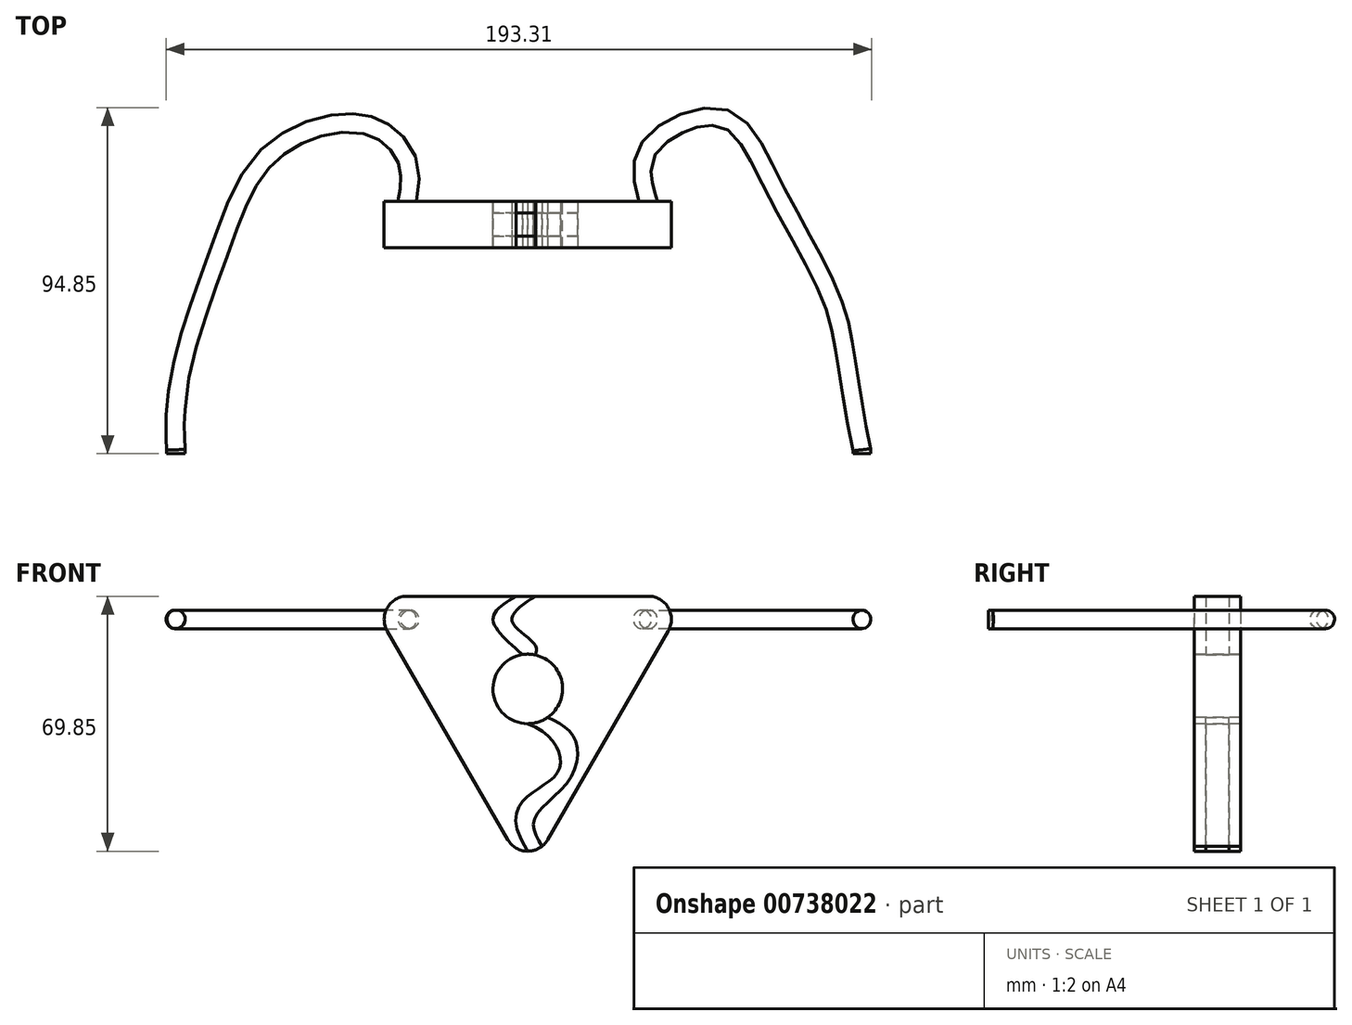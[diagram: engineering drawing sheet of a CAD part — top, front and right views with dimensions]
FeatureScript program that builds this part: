
annotation { "Feature Type Name" : "Feature", "Feature Type Description" : "" }
export const myFeature = defineFeature(function(context is Context, id is Id, definition is map)
    precondition{}
    {
        {
            var Q0;
            Q0=qCreatedBy(makeId("Front.planeOp"),FACE);
            var sketch = newSketch(context, id + "F0", { "sketchPlane" : qUnion([Q0])});
            skCircle(sketch, "E0", {"center": v(0, 0) * mm, "radius": 9.53 * mm});
            skLineSegment(sketch, "E1", {"start": v(-33, 25.4) * mm, "end": v(33, 25.4) * mm});
            skLineSegment(sketch, "E2", {"start": v(38.5, 15.88) * mm, "end": v(5.5, -41.27) * mm});
            skLineSegment(sketch, "E3", {"start": v(-5.5, -41.27) * mm, "end": v(-38.5, 15.87) * mm});
            skPoint(sketch, "E4.visualSharp", {"position": v(-44, 25.4) * mm});
            skArc(sketch, "E4.filletArc", {"start": v(-33, 25.4) * mm, "mid": v(-38.5, 22.23) * mm, "end": v(-38.5, 15.88) * mm});
            skPoint(sketch, "E5.visualSharp", {"position": v(44, 25.4) * mm});
            skArc(sketch, "E5.filletArc", {"start": v(38.5, 15.88) * mm, "mid": v(38.5, 22.23) * mm, "end": v(33, 25.4) * mm});
            skPoint(sketch, "E6.visualSharp", {"position": v(0, -50.8) * mm});
            skArc(sketch, "E6.filletArc", {"start": v(-5.5, -41.27) * mm, "mid": v(0, -44.45) * mm, "end": v(5.5, -41.27) * mm});
            skPoint(sketch, "E7.2.internal.snap0", {"position": v(0, 25.4) * mm});
            skFitSpline(sketch, "E8", {"points": [v(0, -9.53) * mm, v(7.61, -23.64) * mm, v(0, -44.45) * mm], "startDerivative": vector(51.93, -20.61) * mm, "endDerivative": vector(51.79, -79.45) * mm});
            skFitSpline(sketch, "E9", {"points": [v(2.14, 25.4) * mm, v(-4.25, 18.42) * mm, v(2.32, 11.47) * mm, v(2.1, 9.3) * mm, v(2.22, 9.26) * mm], "startDerivative": vector(-27.78, -18.05) * mm, "endDerivative": vector(3.6, 0.43) * mm});
            skFitSpline(sketch, "E10", {"points": [v(-3.19, 25.4) * mm, v(-9.52, 19.35) * mm, v(-1.43, 9.42) * mm], "startDerivative": vector(-20.5, -12.29) * mm, "endDerivative": vector(22.65, -19.45) * mm});
            skFitSpline(sketch, "E11", {"points": [v(3.94, -43.08) * mm, v(1.78, -35.75) * mm, v(11.53, -24.63) * mm, v(12.73, -13.34) * mm, v(5.5, -7.78) * mm], "startDerivative": vector(-21.2, 34.46) * mm, "endDerivative": vector(-37.55, 18.63) * mm});
            skSolve(sketch);
        }
        {
            var Q0;
            Q0 = qSketchRegion(id + "F0", true);
            extrude(context, id + "F1", {"entities" : qUnion([Q0]), "endBound" : BoundingType.SYMMETRIC, "depth" : 12.7 * mm, "offsetDistance" : 25.4 * mm});
        }
        {
            var Q0;
            {var subQ0=sQuery(id+"F0.wireOp",EDGE,"E10");Q0=makeQuery(id+"F0.imprint","IMPRINT",FACE,{"disambiguationData":[TD([[makeQuery(id+"F0.imprint","IMPRINT",EDGE,{"derivedFrom":subQ0}),1.0]])]});}
            var Q1;
            {var subQ0=sQuery(id+"F0.wireOp",EDGE,"E8");Q1=makeQuery(id+"F0.imprint","IMPRINT",FACE,{"disambiguationData":[TD([[makeQuery(id+"F0.imprint","IMPRINT",EDGE,{"derivedFrom":subQ0}),1.0]])]});}
            extrude(context, id + "F2", {"entities" : qUnion([Q0, Q1]), "operationType" : NewBodyOperationType.REMOVE, "endBound" : BoundingType.SYMMETRIC, "oppositeDirection" : true, "depth" : 25.4 * mm, "offsetDistance" : 25.4 * mm});
        }
        {
            var Q0;
            {var subQ0=sQuery(id+"F0.wireOp",EDGE,"E10");Q0=makeQuery(id+"F0.imprint","IMPRINT",FACE,{"disambiguationData":[TD([[makeQuery(id+"F0.imprint","IMPRINT",EDGE,{"derivedFrom":subQ0}),1.0]])]});}
            var Q1;
            {var subQ0=sQuery(id+"F0.wireOp",EDGE,"E8");Q1=makeQuery(id+"F0.imprint","IMPRINT",FACE,{"disambiguationData":[TD([[makeQuery(id+"F0.imprint","IMPRINT",EDGE,{"derivedFrom":subQ0}),1.0]])]});}
            extrude(context, id + "F3", {"entities" : qUnion([Q0, Q1]), "endBound" : BoundingType.SYMMETRIC, "depth" : 6.35 * mm, "offsetDistance" : 25.4 * mm});
        }
        {
            var Q0;
            {var subQ0=sQuery(id+"F0.wireOp",EDGE,"E4.filletArc");var subQ1=sQuery(id+"F0.wireOp",EDGE,"E1");var subQ2=sQuery(id+"F0.wireOp",EDGE,"E3");var subQ3=sQuery(id+"F0.wireOp",EDGE,"E0");var subQ4=sQuery(id+"F0.wireOp",EDGE,"E6.filletArc");Q0=makeQuery(id+"F2.boolean.opBoolean","SPLIT",FACE,{"disambiguationData":[TD([makeQuery(id+"F1.opExtrude","SWEPT_FACE",FACE,{"disambiguationData":[OSD([subQ2])]})])],"derivedFrom":makeQuery(id+"F1.opExtrude","CAP_FACE",FACE,{"disambiguationData":[OSD([subQ3,subQ1,sQuery(id+"F0.wireOp",EDGE,"E2"),subQ2,subQ0,sQuery(id+"F0.wireOp",EDGE,"E5.filletArc"),subQ4])],"isStart":true})});}
            var sketch = newSketch(context, id + "F4", { "sketchPlane" : qUnion([Q0])});
            skCircle(sketch, "E12", {"center": v(33, 19.05) * mm, "radius": 2.54 * mm});
            skSolve(sketch);
        }
        {
            var Q0;
            Q0=qCreatedBy(makeId("Top.planeOp"),FACE);
            var sketch = newSketch(context, id + "F5", { "sketchPlane" : qUnion([Q0])});
            skPoint(sketch, "E13.0", {"position": v(-33, 6.35) * mm});
            skLineSegment(sketch, "E14.0", {"start": v(-35.54, 6.35) * mm, "end": v(-30.46, 6.35) * mm});
            skFitSpline(sketch, "E15", {"points": [v(-33, 6.35) * mm, v(-33, 17.32) * mm, v(-43.99, 27.32) * mm, v(-69.53, 20.42) * mm, v(-84, -5.7) * mm, v(-94.93, -39.8) * mm, v(-96.4, -61.63) * mm], "startDerivative": vector(15.54, 93.73) * mm, "endDerivative": vector(8.7, -120.43) * mm});
            skLineSegment(sketch, "E16", {"start": v(-96.4, -61.63) * mm, "end": v(-96.4, -64.8) * mm});
            skSolve(sketch);
        }
        {
            var Q0;
            Q0=makeQuery(id+"F4.imprint","IMPRINT",FACE,{"disambiguationData":[TD([[makeQuery(id+"F4.imprint","IMPRINT",EDGE,{"derivedFrom":sQuery(id+"F4.wireOp",EDGE,"E12")}),1.0]])]});
            var Q1;
            Q1=sQuery(id+"F5.wireOp",EDGE,"E15");
            var Q2;
            Q2=sQuery(id+"F5.wireOp",EDGE,"E16");
            sweep(context, id + "F6", {"profiles" : qUnion([Q0]), "path" : qUnion([Q1, Q2])});
        }
        {
            var Q0;
            {var subQ0=sQuery(id+"F0.wireOp",EDGE,"E5.filletArc");var subQ1=sQuery(id+"F0.wireOp",EDGE,"E2");var subQ2=sQuery(id+"F0.wireOp",EDGE,"E1");var subQ3=sQuery(id+"F0.wireOp",EDGE,"E0");var subQ4=sQuery(id+"F0.wireOp",EDGE,"E6.filletArc");Q0=makeQuery(id+"F2.boolean.opBoolean","SPLIT",FACE,{"disambiguationData":[TD([makeQuery(id+"F1.opExtrude","SWEPT_FACE",FACE,{"disambiguationData":[OSD([subQ1])]})])],"derivedFrom":makeQuery(id+"F1.opExtrude","CAP_FACE",FACE,{"disambiguationData":[OSD([subQ3,subQ2,subQ1,sQuery(id+"F0.wireOp",EDGE,"E3"),sQuery(id+"F0.wireOp",EDGE,"E4.filletArc"),subQ0,subQ4])],"isStart":true})});}
            var sketch = newSketch(context, id + "F7", { "sketchPlane" : qUnion([Q0])});
            skCircle(sketch, "E17", {"center": v(-33, 19.05) * mm, "radius": 2.54 * mm});
            skSolve(sketch);
        }
        {
            var Q0;
            Q0=qCreatedBy(makeId("Top.planeOp"),FACE);
            var sketch = newSketch(context, id + "F8", { "sketchPlane" : qUnion([Q0])});
            skLineSegment(sketch, "E18.0", {"start": v(30.46, 6.35) * mm, "end": v(35.54, 6.35) * mm});
            skPoint(sketch, "E19.1.internal.snap0", {"position": v(33, 6.35) * mm});
            skPoint(sketch, "E19.5.internal.snap0", {"position": v(33, 6.35) * mm});
            skFitSpline(sketch, "E20.0", {"points": [v(-33, 6.35) * mm, v(-32.4, 9.99) * mm, v(-31.07, 17.93) * mm, v(-43.46, 31.53) * mm, v(-74, 23.13) * mm, v(-83.82, -5.79) * mm, v(-96.37, -38.97) * mm, v(-96.87, -55.02) * mm, v(-96.4, -61.63) * mm]});
            skLineSegment(sketch, "E21", {"start": v(-96.4, -61.63) * mm, "end": v(91.56, -61.63) * mm, "construction": true});
            skFitSpline(sketch, "E22", {"points": [v(33, 6.35) * mm, v(33, 20.71) * mm, v(52.72, 29.42) * mm, v(66.28, 12.48) * mm, v(82.5, -18.5) * mm, v(86.85, -34.47) * mm, v(91.56, -61.63) * mm], "startDerivative": vector(-31.66, 110.98) * mm, "endDerivative": vector(35.2, -154.03) * mm});
            skLineSegment(sketch, "E23", {"start": v(-96.4, -61.63) * mm, "end": v(-96.4, -63.53) * mm});
            skLineSegment(sketch, "E24", {"start": v(91.56, -61.63) * mm, "end": v(91.56, -64.8) * mm});
            skSolve(sketch);
        }
        {
            var Q0;
            Q0=makeQuery(id+"F7.imprint","IMPRINT",FACE,{"disambiguationData":[TD([[makeQuery(id+"F7.imprint","IMPRINT",EDGE,{"derivedFrom":sQuery(id+"F7.wireOp",EDGE,"E17")}),1.0]])]});
            var Q1;
            Q1=sQuery(id+"F8.wireOp",EDGE,"E22");
            var Q2;
            Q2=sQuery(id+"F8.wireOp",EDGE,"E24");
            sweep(context, id + "F9", {"profiles" : qUnion([Q0]), "path" : qUnion([Q1, Q2])});
        }
        {
            var Q0;
            Q0=qCreatedBy(makeId("Top.planeOp"),FACE);
            var sketch = newSketch(context, id + "F10", { "sketchPlane" : qUnion([Q0])});
            skLineSegment(sketch, "E25", {"start": v(0, -62.67) * mm, "end": v(110.98, -62.67) * mm});
            skLineSegment(sketch, "E26", {"start": v(110.98, -62.67) * mm, "end": v(110.98, -71.42) * mm});
            skLineSegment(sketch, "E27", {"start": v(110.98, -71.42) * mm, "end": v(-117.15, -71.42) * mm});
            skLineSegment(sketch, "E28", {"start": v(-117.15, -71.42) * mm, "end": v(-117.15, -62.67) * mm});
            skLineSegment(sketch, "E29", {"start": v(-117.15, -62.67) * mm, "end": v(0, -62.67) * mm});
            skSolve(sketch);
        }
        {
            var Q0;
            Q0 = qSketchRegion(id + "F10", true);
            extrude(context, id + "F11", {"entities" : qUnion([Q0]), "operationType" : NewBodyOperationType.REMOVE, "depth" : 25.4 * mm, "offsetDistance" : 25.4 * mm});
        }
    });
